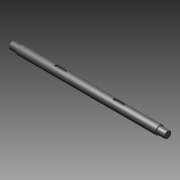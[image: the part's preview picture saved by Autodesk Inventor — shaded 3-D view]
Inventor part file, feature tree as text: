
AUTODESK INVENTOR PART (.ipt)
format: ipt  version: 2011 SP1 (Build 150282100, 282)  size: 129,536 bytes
history: native  units: mm
features: extrude x2, revolve x1, sketch x1
ambient origin geometry x8: Origin, YZ Plane, XZ Plane, XY Plane, X Axis, Y Axis, Z Axis, Center Point
bodies: Solid1 (feature_tree)
feature tree (4):
  revolve  "Revolution1"  [1 undecoded]
  extrude  "Extrusion1"  Depth=3.0mm TaperAngle=0.0deg
  extrude  "Extrusion2"  [1 undecoded]
  sketch  "Sketch_1"  dims[d0=360.0deg d1=3.0mm d2=0.0mm d3=3.0mm d4=0.0mm]
note: 2 required parameter values undecoded (feature->parameter linkage not recoverable at this tier; creation-order binding heuristic only, values carry confidence <= 0.55)